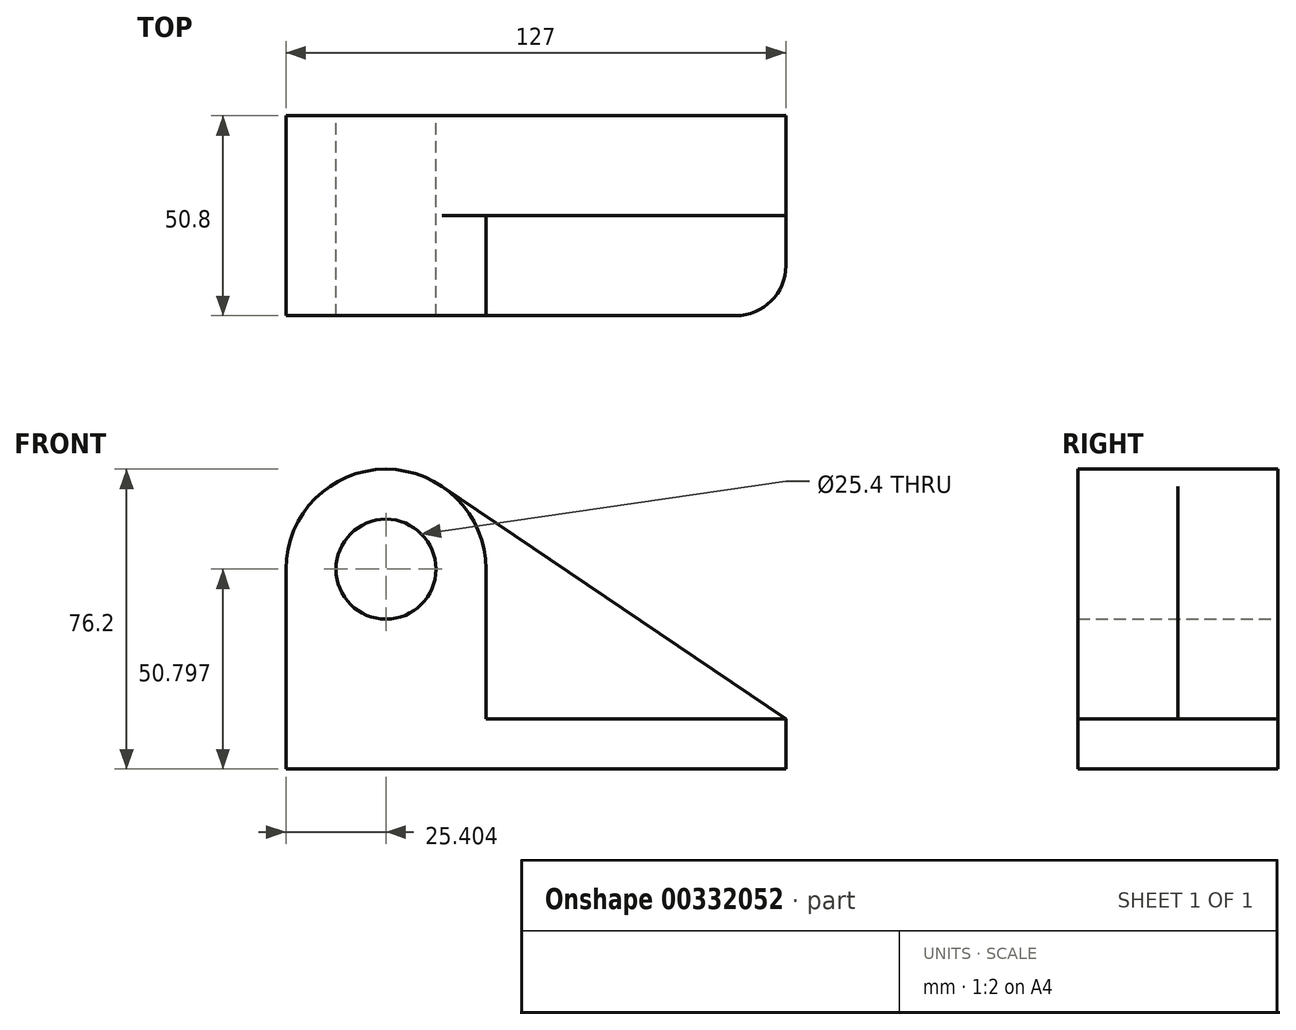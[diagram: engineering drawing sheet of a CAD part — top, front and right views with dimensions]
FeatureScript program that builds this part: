
annotation { "Feature Type Name" : "Feature", "Feature Type Description" : "" }
export const myFeature = defineFeature(function(context is Context, id is Id, definition is map)
    precondition{}
    {
        {
            var Q0;
            Q0=qCreatedBy(makeId("Front.planeOp"),FACE);
            var sketch = newSketch(context, id + "F0", { "sketchPlane" : qUnion([Q0])});
            skCircle(sketch, "E0", {"center": v(-37.9, 24.7) * mm, "radius": 12.7 * mm});
            skLineSegment(sketch, "E1", {"start": v(-63.3, 24.7) * mm, "end": v(-63.3, -26.1) * mm});
            skPoint(sketch, "E2.start.orphan", {"position": v(-12.5, 24.7) * mm});
            skLineSegment(sketch, "E3.bottom", {"start": v(-63.3, -26.1) * mm, "end": v(63.7, -26.1) * mm});
            skLineSegment(sketch, "E3.top", {"start": v(-63.3, -26.1) * mm, "end": v(63.7, -26.1) * mm});
            skLineSegment(sketch, "E3.left", {"start": v(-63.3, -26.1) * mm, "end": v(-63.3, -26.1) * mm});
            skLineSegment(sketch, "E3.right", {"start": v(63.7, -26.1) * mm, "end": v(63.7, -26.1) * mm});
            skLineSegment(sketch, "E4", {"start": v(63.7, -26.1) * mm, "end": v(63.7, -13.4) * mm});
            skPoint(sketch, "E5.endSnap0", {"position": v(-23.71, 45.68) * mm});
            skPoint(sketch, "E5.end.orphan", {"position": v(-23.71, 46.75) * mm});
            skLineSegment(sketch, "E6", {"start": v(63.7, -13.4) * mm, "end": v(-23.66, 45.73) * mm});
            skArc(sketch, "E7", {"start": v(-23.66, 45.73) * mm, "mid": v(-49.8, 47.13) * mm, "end": v(-63.3, 24.7) * mm});
            skSolve(sketch);
        }
        {
            var Q0;
            Q0=makeQuery(id+"F0.imprint","IMPRINT",FACE,{"disambiguationData":[TD([[makeQuery(id+"F0.imprint","IMPRINT",EDGE,{"derivedFrom":sQuery(id+"F0.wireOp",EDGE,"E0")}),-1.0]])]});
            extrude(context, id + "F1", {"entities" : qUnion([Q0]), "depth" : 25.4 * mm});
        }
        {
            var Q0;
            Q0=makeQuery(id+"F1.opExtrude","CAP_FACE",FACE,{"disambiguationData":[OSD([sQuery(id+"F0.wireOp",EDGE,"E0"),sQuery(id+"F0.wireOp",EDGE,"E1"),sQuery(id+"F0.wireOp",EDGE,"E3.top"),sQuery(id+"F0.wireOp",EDGE,"E4"),sQuery(id+"F0.wireOp",EDGE,"E6"),sQuery(id+"F0.wireOp",EDGE,"E7")])],"isStart":false});
            var sketch = newSketch(context, id + "F2", { "sketchPlane" : qUnion([Q0])});
            skCircle(sketch, "E8", {"center": v(-37.9, 24.7) * mm, "radius": 12.7 * mm});
            skArc(sketch, "E9", {"start": v(-12.5, 24.7) * mm, "mid": v(-37.9, 50.1) * mm, "end": v(-63.3, 24.7) * mm});
            skLineSegment(sketch, "E10.top", {"start": v(63.7, -26.1) * mm, "end": v(-63.3, -26.1) * mm});
            skLineSegment(sketch, "E10.left", {"start": v(63.7, -13.4) * mm, "end": v(63.7, -26.1) * mm});
            skLineSegment(sketch, "E10.right", {"start": v(-63.3, -13.4) * mm, "end": v(-63.3, -26.1) * mm});
            skLineSegment(sketch, "E11.bottom", {"start": v(63.7, -13.4) * mm, "end": v(-12.5, -13.4) * mm});
            skLineSegment(sketch, "E12", {"start": v(-63.3, 24.7) * mm, "end": v(-63.3, -26.1) * mm});
            skLineSegment(sketch, "E13", {"start": v(-12.5, 24.7) * mm, "end": v(-12.5, -13.4) * mm});
            skSolve(sketch);
        }
        {
            var Q0;
            Q0=makeQuery(id+"F2.imprint","IMPRINT",FACE,{"disambiguationData":[TD([[makeQuery(id+"F2.imprint","IMPRINT",EDGE,{"derivedFrom":sQuery(id+"F2.wireOp",EDGE,"E8")}),-1.0]])]});
            extrude(context, id + "F3", {"entities" : qUnion([Q0]), "operationType" : NewBodyOperationType.ADD, "depth" : 25.4 * mm});
        }
        {
            var Q0;
            Q0=makeQuery(id+"F3.opExtrude","CAP_EDGE",EDGE,{"disambiguationData":[OSD([sQuery(id+"F2.wireOp",EDGE,"E10.left")])],"isStart":false});
            fillet(context, id + "F4", {"entities" : qUnion([Q0]), "radius" : 12.7 * mm, "tangentPropagation" : true, "allowEdgeOverflow" : false});
        }
    });
